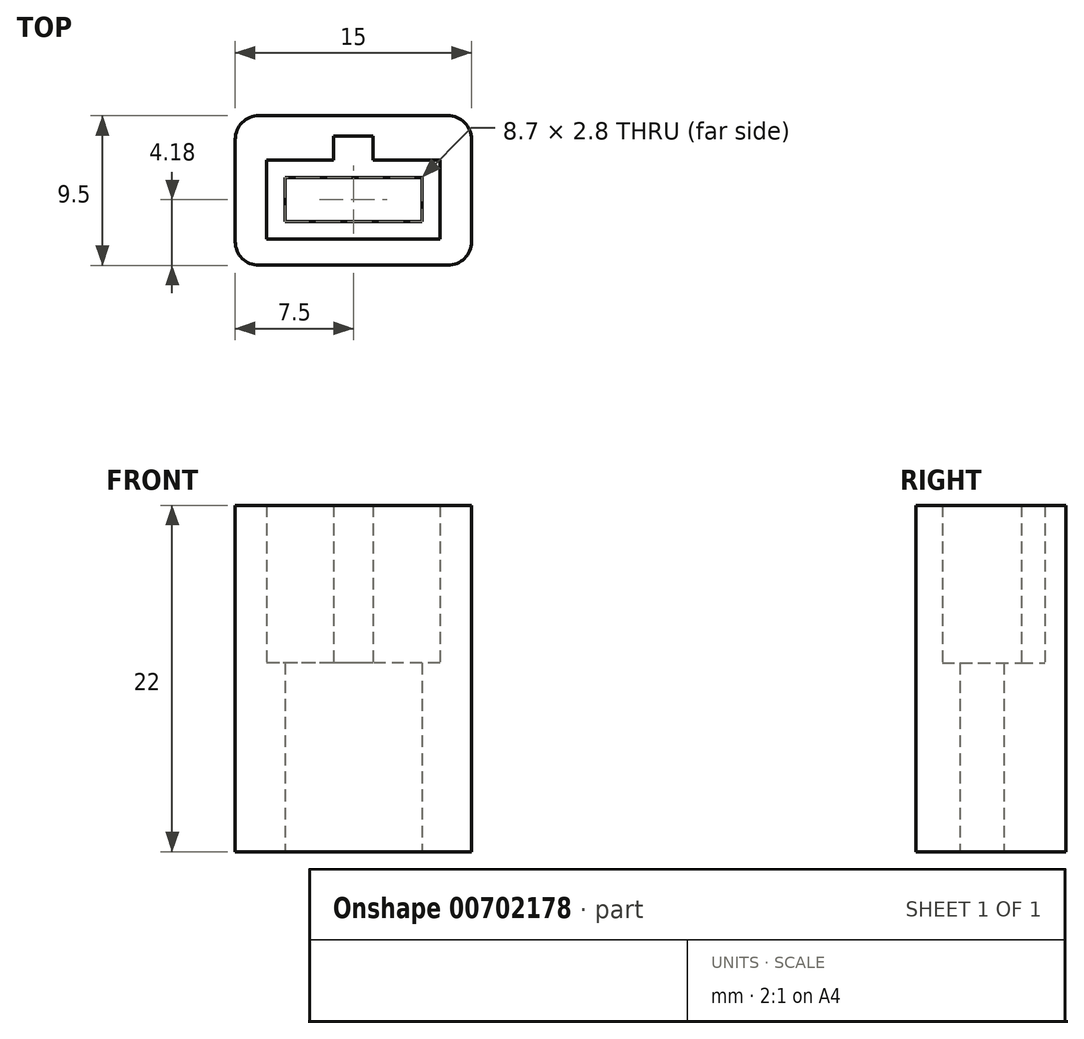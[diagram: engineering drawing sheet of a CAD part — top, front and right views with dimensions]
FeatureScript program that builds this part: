
annotation { "Feature Type Name" : "Feature", "Feature Type Description" : "" }
export const myFeature = defineFeature(function(context is Context, id is Id, definition is map)
    precondition{}
    {
        {
            var Q0;
            Q0=qCreatedBy(makeId("Top.planeOp"),FACE);
            var sketch = newSketch(context, id + "F0", { "sketchPlane" : qUnion([Q0])});
            skPoint(sketch, "E0.middle", {"position": v(0, 0) * mm});
            skLineSegment(sketch, "E1.bottom", {"start": v(5.5, -2.5) * mm, "end": v(-5.5, -2.5) * mm});
            skLineSegment(sketch, "E1.top", {"start": v(5.5, 2.5) * mm, "end": v(1.25, 2.5) * mm});
            skLineSegment(sketch, "E1.left", {"start": v(5.5, -2.5) * mm, "end": v(5.5, 2.5) * mm});
            skLineSegment(sketch, "E1.right", {"start": v(-5.5, -2.5) * mm, "end": v(-5.5, 2.5) * mm});
            skLineSegment(sketch, "E2.top", {"start": v(1.25, 4.01) * mm, "end": v(-1.25, 4.01) * mm});
            skLineSegment(sketch, "E2.left", {"start": v(1.25, 2.5) * mm, "end": v(1.25, 4.01) * mm});
            skLineSegment(sketch, "E2.right", {"start": v(-1.25, 2.5) * mm, "end": v(-1.25, 4.01) * mm});
            skPoint(sketch, "E2.middle", {"position": v(0, 3.26) * mm});
            skPoint(sketch, "E2.middle.positionSnap0", {"position": v(0, 2.5) * mm});
            skPoint(sketch, "E2.centerSnap0", {"position": v(0, 2.5) * mm});
            skLineSegment(sketch, "E3.bottom", {"start": v(7.5, -4.18) * mm, "end": v(-7.5, -4.18) * mm});
            skLineSegment(sketch, "E3.top", {"start": v(7.5, 5.32) * mm, "end": v(-7.5, 5.32) * mm});
            skLineSegment(sketch, "E3.left", {"start": v(7.5, -4.18) * mm, "end": v(7.5, 5.32) * mm});
            skLineSegment(sketch, "E3.right", {"start": v(-7.5, -4.18) * mm, "end": v(-7.5, 5.32) * mm});
            skPoint(sketch, "E3.middle", {"position": v(0, 0.57) * mm});
            skLineSegment(sketch, "E4.trimOffspring", {"start": v(-1.25, 2.5) * mm, "end": v(-5.5, 2.5) * mm});
            skLineSegment(sketch, "E5.bottom", {"start": v(4.35, -1.4) * mm, "end": v(-4.35, -1.4) * mm});
            skLineSegment(sketch, "E5.top", {"start": v(4.35, 1.4) * mm, "end": v(-4.35, 1.4) * mm});
            skLineSegment(sketch, "E5.left", {"start": v(4.35, -1.4) * mm, "end": v(4.35, 1.4) * mm});
            skLineSegment(sketch, "E5.right", {"start": v(-4.35, -1.4) * mm, "end": v(-4.35, 1.4) * mm});
            skSolve(sketch);
        }
        {
            var Q0;
            Q0=makeQuery(id+"F0.imprint","IMPRINT",FACE,{"disambiguationData":[TD([[makeQuery(id+"F0.imprint","IMPRINT",EDGE,{"derivedFrom":sQuery(id+"F0.wireOp",EDGE,"E1.bottom")}),1.0]])]});
            extrude(context, id + "F1", {"entities" : qUnion([Q0]), "depth" : 22 * mm, "offsetDistance" : 25 * mm});
        }
        {
            var Q0;
            Q0=makeQuery(id+"F0.imprint","IMPRINT",FACE,{"disambiguationData":[TD([[makeQuery(id+"F0.imprint","IMPRINT",EDGE,{"derivedFrom":sQuery(id+"F0.wireOp",EDGE,"E1.bottom")}),-1.0]])]});
            extrude(context, id + "F2", {"entities" : qUnion([Q0]), "operationType" : NewBodyOperationType.ADD, "depth" : 12 * mm, "offsetDistance" : 25 * mm});
        }
        {
            var Q0;
            Q0=makeQuery(id+"F1.opExtrude","SWEPT_EDGE",EDGE,{"disambiguationData":[OSD([sQuery(id+"F0.wireOp",EDGE,"E3.top"),sQuery(id+"F0.wireOp",EDGE,"E3.right")])]});
            var Q1;
            Q1=makeQuery(id+"F1.opExtrude","SWEPT_EDGE",EDGE,{"disambiguationData":[OSD([sQuery(id+"F0.wireOp",EDGE,"E3.top"),sQuery(id+"F0.wireOp",EDGE,"E3.left")])]});
            var Q2;
            Q2=makeQuery(id+"F1.opExtrude","SWEPT_EDGE",EDGE,{"disambiguationData":[OSD([sQuery(id+"F0.wireOp",EDGE,"E3.bottom"),sQuery(id+"F0.wireOp",EDGE,"E3.left")])]});
            var Q3;
            Q3=makeQuery(id+"F1.opExtrude","SWEPT_EDGE",EDGE,{"disambiguationData":[OSD([sQuery(id+"F0.wireOp",EDGE,"E3.bottom"),sQuery(id+"F0.wireOp",EDGE,"E3.right")])]});
            fillet(context, id + "F3", {"entities" : qUnion([Q0, Q1, Q2, Q3]), "radius" : 1.5 * mm, "tangentPropagation" : true, "allowEdgeOverflow" : false});
        }
    });
